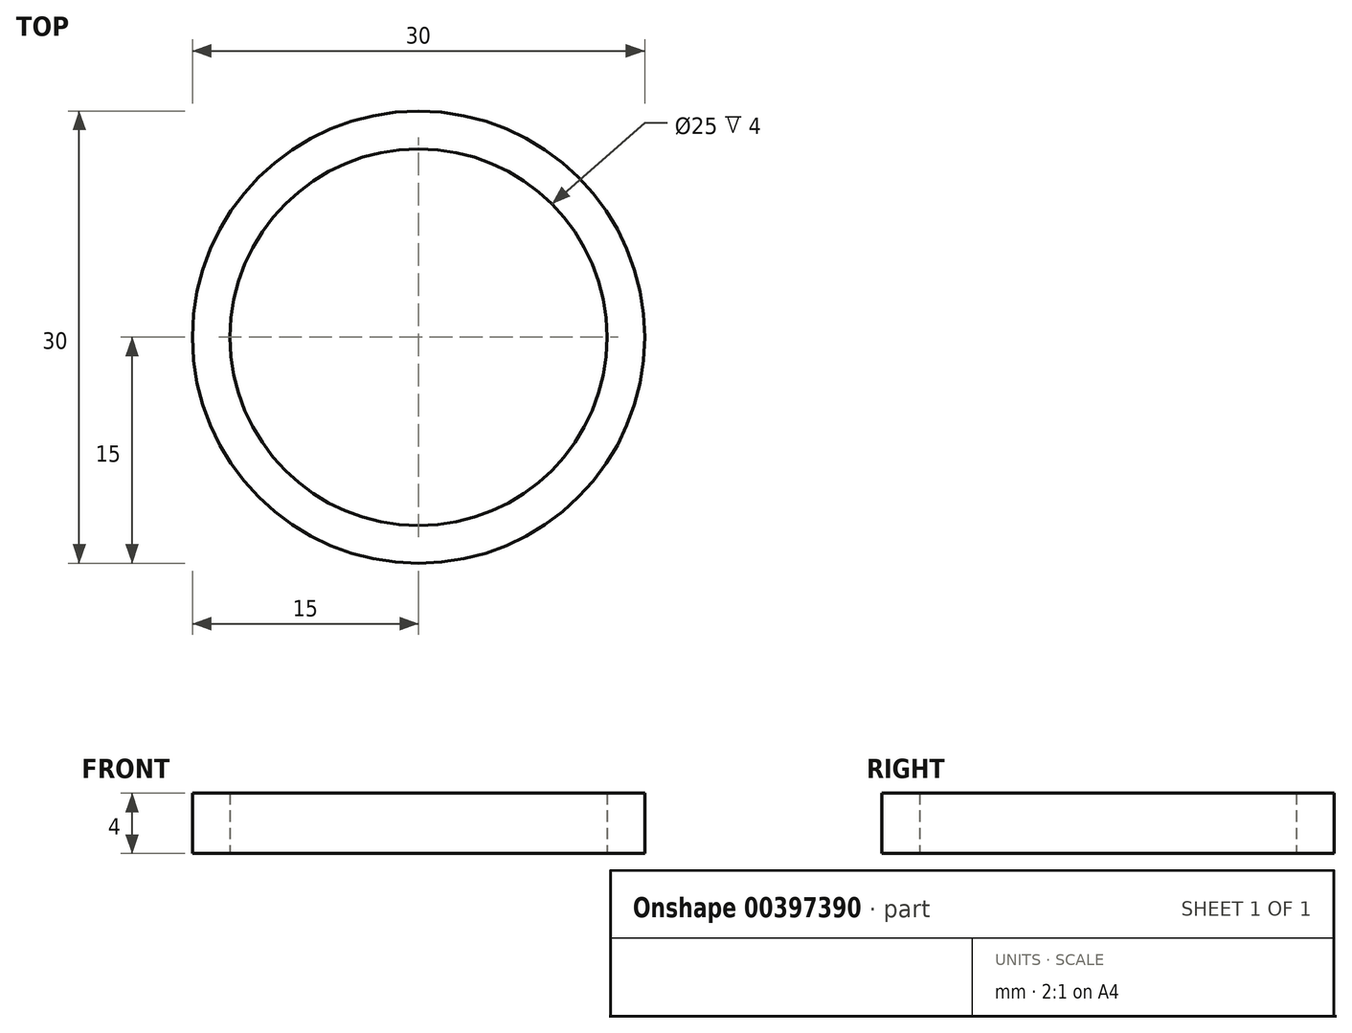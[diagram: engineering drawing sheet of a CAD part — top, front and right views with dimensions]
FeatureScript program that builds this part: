
annotation { "Feature Type Name" : "Feature", "Feature Type Description" : "" }
export const myFeature = defineFeature(function(context is Context, id is Id, definition is map)
    precondition{}
    {
        {
            var Q0;
            Q0=qCreatedBy(makeId("Top.planeOp"),FACE);
            var sketch = newSketch(context, id + "F0", { "sketchPlane" : qUnion([Q0])});
            skCircle(sketch, "E0", {"center": v(0, 0) * mm, "radius": 15 * mm});
            skCircle(sketch, "E1", {"center": v(0, 0) * mm, "radius": 12.5 * mm});
            skSolve(sketch);
        }
        {
            var Q0;
            Q0=makeQuery(id+"F0.imprint","IMPRINT",FACE,{"disambiguationData":[TD([[makeQuery(id+"F0.imprint","IMPRINT",EDGE,{"derivedFrom":sQuery(id+"F0.wireOp",EDGE,"E0")}),1.0]])]});
            extrude(context, id + "F1", {"entities" : qUnion([Q0]), "depth" : 4 * mm});
        }
    });
